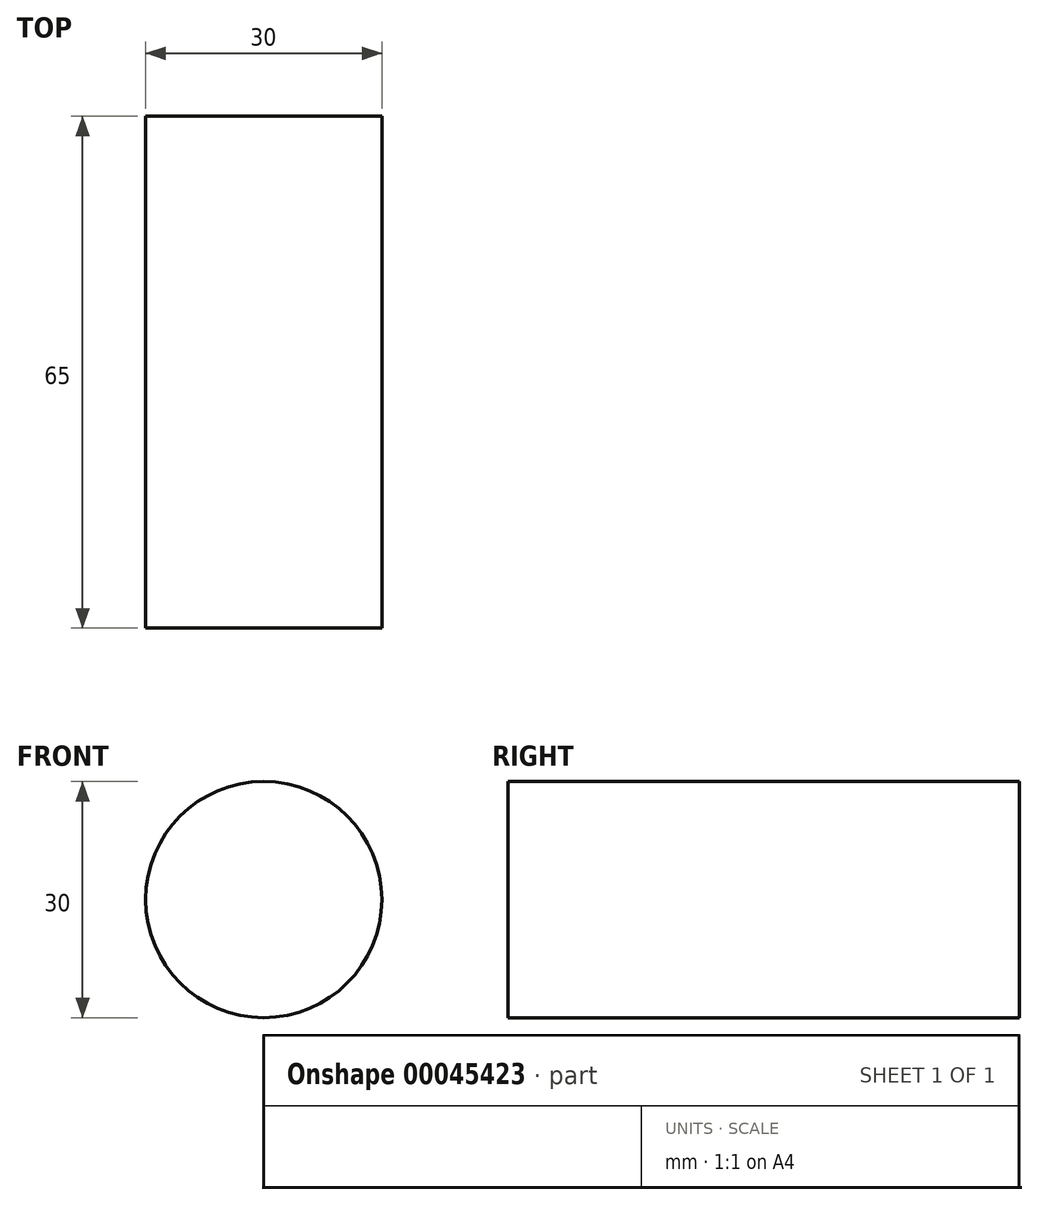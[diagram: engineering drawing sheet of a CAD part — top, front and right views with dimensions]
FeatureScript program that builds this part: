
annotation { "Feature Type Name" : "Feature", "Feature Type Description" : "" }
export const myFeature = defineFeature(function(context is Context, id is Id, definition is map)
    precondition{}
    {
        {
            var Q0;
            Q0=qCreatedBy(makeId("Front.planeOp"),FACE);
            var sketch = newSketch(context, id + "F0", { "sketchPlane" : qUnion([Q0])});
            skCircle(sketch, "E0", {"center": v(0, 0) * mm, "radius": 15 * mm});
            skSolve(sketch);
        }
        {
            var Q0;
            Q0 = qSketchRegion(id + "F0", true);
            extrude(context, id + "F1", {"entities" : qUnion([Q0]), "oppositeDirection" : true, "depth" : 65 * mm});
        }
    });
